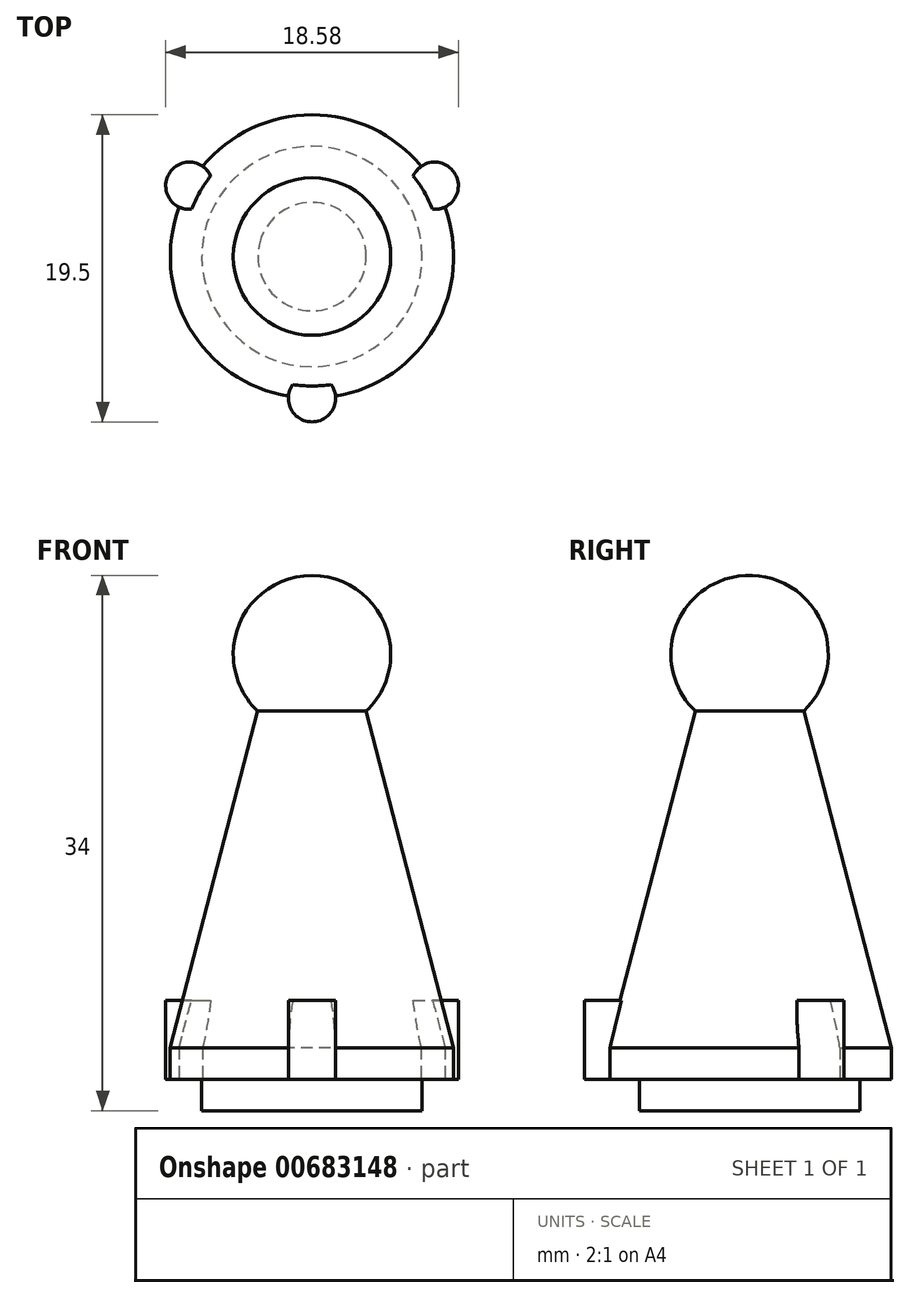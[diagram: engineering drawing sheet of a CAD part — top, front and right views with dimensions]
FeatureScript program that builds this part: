
annotation { "Feature Type Name" : "Feature", "Feature Type Description" : "" }
export const myFeature = defineFeature(function(context is Context, id is Id, definition is map)
    precondition{}
    {
        {
            var Q0;
            Q0=qCreatedBy(makeId("Top.planeOp"),FACE);
            var sketch = newSketch(context, id + "F0", { "sketchPlane" : qUnion([Q0])});
            skCircle(sketch, "E0", {"center": v(0, 0) * mm, "radius": 7 * mm});
            skSolve(sketch);
        }
        {
            var Q0;
            Q0=makeQuery(id+"F0.imprint","IMPRINT",FACE,{"disambiguationData":[TD([[makeQuery(id+"F0.imprint","IMPRINT",EDGE,{"derivedFrom":sQuery(id+"F0.wireOp",EDGE,"E0")}),1.0]])]});
            extrude(context, id + "F1", {"entities" : qUnion([Q0]), "depth" : 2 * mm, "offsetDistance" : 25 * mm});
        }
        {
            var Q0;
            Q0=makeQuery(id+"F1.opExtrude","CAP_FACE",FACE,{"disambiguationData":[OSD([sQuery(id+"F0.wireOp",EDGE,"E0")])],"isStart":false});
            var sketch = newSketch(context, id + "F2", { "sketchPlane" : qUnion([Q0])});
            skCircle(sketch, "E1", {"center": v(0, 0) * mm, "radius": 9 * mm});
            skSolve(sketch);
        }
        {
            var Q0;
            Q0=makeQuery(id+"F2.imprint","IMPRINT",FACE,{"disambiguationData":[TD([[makeQuery(id+"F2.imprint","IMPRINT",EDGE,{"derivedFrom":sQuery(id+"F2.wireOp",EDGE,"E1")}),1.0]])]});
            var Q1;
            Q1=makeQuery(id+"F2.imprint","IMPRINT",FACE,{"disambiguationData":[TD([[makeQuery(id+"F2.imprint","IMPRINT",EDGE,{"derivedFrom":makeQuery(id+"F1.opExtrude","CAP_EDGE",EDGE,{"disambiguationData":[OSD([sQuery(id+"F0.wireOp",EDGE,"E0")])],"isStart":false})}),1.0]])]});
            extrude(context, id + "F3", {"entities" : qUnion([Q0, Q1]), "operationType" : NewBodyOperationType.ADD, "depth" : 2 * mm, "offsetDistance" : 25 * mm});
        }
        {
            var Q0;
            Q0=makeQuery(id+"F3.opExtrude","CAP_FACE",FACE,{"disambiguationData":[OSD([sQuery(id+"F2.wireOp",EDGE,"E1")])],"isStart":false});
            cPlane(context, id + "F4", {"entities" : qUnion([Q0]), "cplaneType" : CPlaneType.OFFSET, "offset" : 25 * mm, "width" : 150 * mm, "height" : 150 * mm});
        }
        {
            var Q0;
            Q0=qCreatedBy(id+"F4.planeOp",FACE);
            var sketch = newSketch(context, id + "F5", { "sketchPlane" : qUnion([Q0])});
            skCircle(sketch, "E2", {"center": v(0, 0) * mm, "radius": 2.5 * mm});
            skSolve(sketch);
        }
        {
            var Q1;
            Q1=makeQuery(id+"F3.opExtrude","CAP_FACE",FACE,{"disambiguationData":[OSD([sQuery(id+"F2.wireOp",EDGE,"E1")])],"isStart":false});
            var Q2;
            Q2=makeQuery(id+"F5.imprint","IMPRINT",FACE,{"disambiguationData":[TD([[makeQuery(id+"F5.imprint","IMPRINT",EDGE,{"derivedFrom":sQuery(id+"F5.wireOp",EDGE,"E2")}),1.0]])]});
            loft(context, id + "F6", {"operationType" : NewBodyOperationType.ADD, "sheetProfilesArray" : [{ "sheetProfileEntities" : qUnion([Q1]) }, { "sheetProfileEntities" : qUnion([Q2]) }]});
        }
        {
            var Q0;
            Q0=makeQuery(id+"F6.opLoft","CAP_FACE",FACE,{"disambiguationData":[OSD([makeQuery(id+"F5.imprint","IMPRINT",FACE,{"disambiguationData":[TD([[makeQuery(id+"F5.imprint","IMPRINT",EDGE,{"derivedFrom":sQuery(id+"F5.wireOp",EDGE,"E2")}),1.0]])]})])],"isStart":true});
            var sketch = newSketch(context, id + "F7", { "sketchPlane" : qUnion([Q0])});
            skCircle(sketch, "E3", {"center": v(0, 0) * mm, "radius": 5 * mm});
            skLineSegment(sketch, "E4", {"start": v(-5, 0) * mm, "end": v(5, 0) * mm});
            skSolve(sketch);
        }
        {
            var Q0;
            {var subQ0=sQuery(id+"F7.wireOp",EDGE,"E4");var subQ1=sQuery(id+"F7.wireOp",EDGE,"E3");var subQ2=makeQuery(id+"F7.imprint","INTERSECT",VERTEX,{"disambiguationData":[OD(0.0)],"derivedFrom":[subQ1,subQ0]});Q0=makeQuery(id+"F7.imprint","IMPRINT",FACE,{"disambiguationData":[TD([[makeQuery(id+"F7.imprint","IMPRINT",EDGE,{"disambiguationData":[TD([[subQ2,-1.0]])],"derivedFrom":subQ1}),1.0]])]});}
            var Q1;
            {var subQ0=sQuery(id+"F7.wireOp",EDGE,"E4");var subQ1=makeQuery(id+"F6.opLoft","MID_CAP_EDGE",EDGE,{"disambiguationData":[OSD([sQuery(id+"F2.wireOp",EDGE,"E1"),sQuery(id+"F5.wireOp",EDGE,"E2")])],"capPos":1.0});var subQ2=makeQuery(id+"F7.imprint","INTERSECT",VERTEX,{"disambiguationData":[OD(0.0)],"derivedFrom":[subQ1,subQ0]});Q1=makeQuery(id+"F7.imprint","IMPRINT",FACE,{"disambiguationData":[TD([[makeQuery(id+"F7.imprint","IMPRINT",EDGE,{"disambiguationData":[TD([[subQ2,-1.0]])],"derivedFrom":subQ0}),-1.0]])]});}
            var Q2;
            Q2=sQuery(id+"F7.wireOp",EDGE,"E4");
            revolve(context, id + "F8", {"operationType" : NewBodyOperationType.ADD, "entities" : qUnion([Q0, Q1]), "axis" : qUnion([Q2]), "revolveType" : RevolveType.FULL});
        }
        {
            var Q0;
            Q0=makeQuery(id+"F3.opExtrude","CAP_FACE",FACE,{"disambiguationData":[OSD([sQuery(id+"F2.wireOp",EDGE,"E1")])],"isStart":true});
            var sketch = newSketch(context, id + "F9", { "sketchPlane" : qUnion([Q0])});
            skCircle(sketch, "E5", {"center": v(0, 9) * mm, "radius": 1.5 * mm});
            skCircle(sketch, "E6.1.0", {"center": v(-7.8, -4.5) * mm, "radius": 1.5 * mm});
            skCircle(sketch, "E6.2.0", {"center": v(7.8, -4.5) * mm, "radius": 1.5 * mm});
            skPoint(sketch, "E6.center", {"position": v(0, 0) * mm});
            skSolve(sketch);
        }
        {
            var Q0;
            {var subQ0=sQuery(id+"F9.wireOp",EDGE,"E5");var subQ1=makeQuery(id+"F3.opExtrude","CAP_EDGE",EDGE,{"disambiguationData":[OSD([sQuery(id+"F2.wireOp",EDGE,"E1")])],"isStart":true});var subQ2=makeQuery(id+"F9.imprint","INTERSECT",VERTEX,{"disambiguationData":[OD(0.0)],"derivedFrom":[subQ1,subQ0]});Q0=makeQuery(id+"F9.imprint","IMPRINT",FACE,{"disambiguationData":[TD([[makeQuery(id+"F9.imprint","IMPRINT",EDGE,{"disambiguationData":[TD([[subQ2,1.0]])],"derivedFrom":subQ0}),1.0]])]});}
            var Q1;
            {var subQ0=sQuery(id+"F9.wireOp",EDGE,"E5");var subQ1=makeQuery(id+"F3.opExtrude","CAP_EDGE",EDGE,{"disambiguationData":[OSD([sQuery(id+"F2.wireOp",EDGE,"E1")])],"isStart":true});var subQ2=makeQuery(id+"F9.imprint","INTERSECT",VERTEX,{"disambiguationData":[OD(0.0)],"derivedFrom":[subQ1,subQ0]});Q1=makeQuery(id+"F9.imprint","IMPRINT",FACE,{"disambiguationData":[TD([[makeQuery(id+"F9.imprint","IMPRINT",EDGE,{"disambiguationData":[TD([[subQ2,-1.0]])],"derivedFrom":subQ0}),1.0]])]});}
            var Q2;
            {var subQ0=sQuery(id+"F9.wireOp",EDGE,"E6.1.0");var subQ1=makeQuery(id+"F3.opExtrude","CAP_EDGE",EDGE,{"disambiguationData":[OSD([sQuery(id+"F2.wireOp",EDGE,"E1")])],"isStart":true});var subQ2=makeQuery(id+"F9.imprint","INTERSECT",VERTEX,{"disambiguationData":[OD(0.0)],"derivedFrom":[subQ1,subQ0]});Q2=makeQuery(id+"F9.imprint","IMPRINT",FACE,{"disambiguationData":[TD([[makeQuery(id+"F9.imprint","IMPRINT",EDGE,{"disambiguationData":[TD([[subQ2,1.0]])],"derivedFrom":subQ0}),1.0]])]});}
            var Q3;
            {var subQ0=sQuery(id+"F9.wireOp",EDGE,"E6.1.0");var subQ1=makeQuery(id+"F3.opExtrude","CAP_EDGE",EDGE,{"disambiguationData":[OSD([sQuery(id+"F2.wireOp",EDGE,"E1")])],"isStart":true});var subQ2=makeQuery(id+"F9.imprint","INTERSECT",VERTEX,{"disambiguationData":[OD(0.0)],"derivedFrom":[subQ1,subQ0]});Q3=makeQuery(id+"F9.imprint","IMPRINT",FACE,{"disambiguationData":[TD([[makeQuery(id+"F9.imprint","IMPRINT",EDGE,{"disambiguationData":[TD([[subQ2,-1.0]])],"derivedFrom":subQ0}),1.0]])]});}
            var Q4;
            {var subQ0=sQuery(id+"F9.wireOp",EDGE,"E6.2.0");var subQ1=makeQuery(id+"F3.opExtrude","CAP_EDGE",EDGE,{"disambiguationData":[OSD([sQuery(id+"F2.wireOp",EDGE,"E1")])],"isStart":true});var subQ2=makeQuery(id+"F9.imprint","INTERSECT",VERTEX,{"disambiguationData":[OD(0.0)],"derivedFrom":[subQ1,subQ0]});Q4=makeQuery(id+"F9.imprint","IMPRINT",FACE,{"disambiguationData":[TD([[makeQuery(id+"F9.imprint","IMPRINT",EDGE,{"disambiguationData":[TD([[subQ2,1.0]])],"derivedFrom":subQ0}),1.0]])]});}
            var Q5;
            {var subQ0=sQuery(id+"F9.wireOp",EDGE,"E6.2.0");var subQ1=makeQuery(id+"F3.opExtrude","CAP_EDGE",EDGE,{"disambiguationData":[OSD([sQuery(id+"F2.wireOp",EDGE,"E1")])],"isStart":true});var subQ2=makeQuery(id+"F9.imprint","INTERSECT",VERTEX,{"disambiguationData":[OD(0.0)],"derivedFrom":[subQ1,subQ0]});Q5=makeQuery(id+"F9.imprint","IMPRINT",FACE,{"disambiguationData":[TD([[makeQuery(id+"F9.imprint","IMPRINT",EDGE,{"disambiguationData":[TD([[subQ2,-1.0]])],"derivedFrom":subQ0}),1.0]])]});}
            extrude(context, id + "F10", {"entities" : qUnion([Q0, Q1, Q2, Q3, Q4, Q5]), "operationType" : NewBodyOperationType.ADD, "oppositeDirection" : true, "depth" : 5 * mm, "offsetDistance" : 25 * mm});
        }
    });
